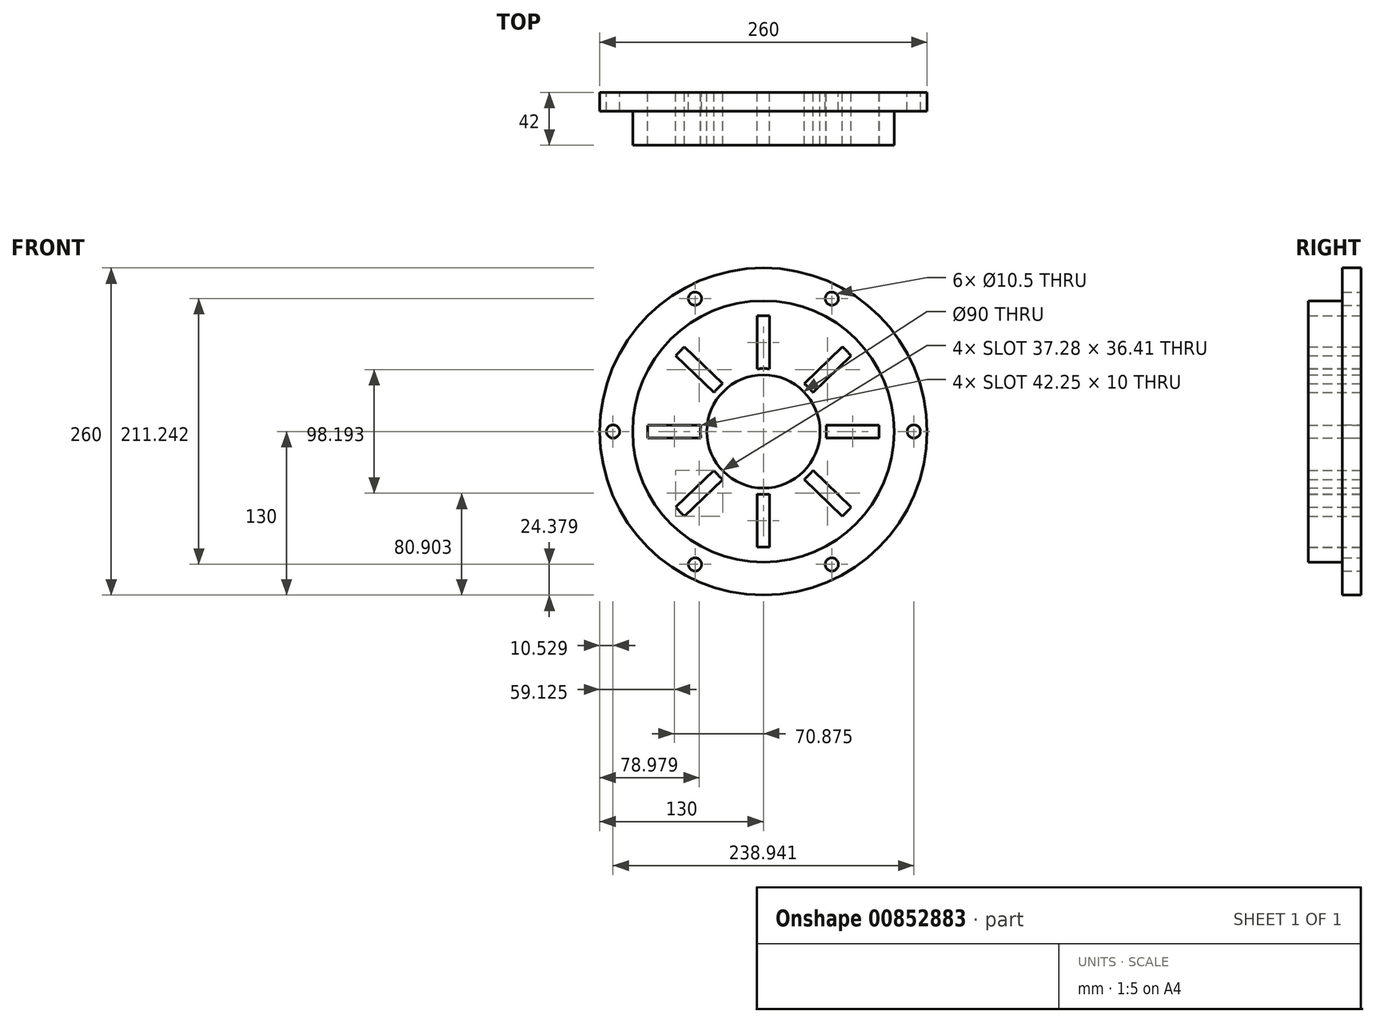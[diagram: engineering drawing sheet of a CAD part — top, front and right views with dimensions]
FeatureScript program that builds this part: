
annotation { "Feature Type Name" : "Feature", "Feature Type Description" : "" }
export const myFeature = defineFeature(function(context is Context, id is Id, definition is map)
    precondition{}
    {
        {
            var Q0;
            Q0=qCreatedBy(makeId("Front.planeOp"),FACE);
            var sketch = newSketch(context, id + "F0", { "sketchPlane" : qUnion([Q0])});
            skCircle(sketch, "E0", {"center": v(0, 0) * mm, "radius": 45 * mm});
            skCircle(sketch, "E1", {"center": v(0, 0) * mm, "radius": 50 * mm});
            skCircle(sketch, "E2", {"center": v(0, 0) * mm, "radius": 92 * mm});
            skCircle(sketch, "E3", {"center": v(0, 0) * mm, "radius": 95 * mm});
            skCircle(sketch, "E4", {"center": v(0, 0) * mm, "radius": 103.9 * mm});
            skCircle(sketch, "E5", {"center": v(0, 0) * mm, "radius": 130 * mm});
            skCircle(sketch, "E6", {"center": v(-54.3, 105.62) * mm, "radius": 5.25 * mm});
            skCircle(sketch, "E7.MirrorC", {"center": v(54.3, 105.62) * mm, "radius": 5.25 * mm});
            skCircle(sketch, "E8.MirrorC", {"center": v(-54.3, -105.62) * mm, "radius": 5.25 * mm});
            skCircle(sketch, "E9.MirrorC", {"center": v(54.3, -105.62) * mm, "radius": 5.25 * mm});
            skLineSegment(sketch, "E10", {"start": v(5, -49.75) * mm, "end": v(5, -91.86) * mm});
            skLineSegment(sketch, "E11.MirrorCS", {"start": v(5, 49.75) * mm, "end": v(5, 91.86) * mm});
            skLineSegment(sketch, "E12.MirrorCS", {"start": v(-5, -49.75) * mm, "end": v(-5, -91.86) * mm});
            skLineSegment(sketch, "E13.MirrorCS", {"start": v(-5, 49.75) * mm, "end": v(-5, 91.86) * mm});
            skLineSegment(sketch, "E14", {"start": v(-49.75, 5) * mm, "end": v(-91.86, 5) * mm});
            skLineSegment(sketch, "E15.MirrorCS", {"start": v(-49.75, -5) * mm, "end": v(-91.86, -5) * mm});
            skLineSegment(sketch, "E16.MirrorCS", {"start": v(49.75, 5) * mm, "end": v(91.86, 5) * mm});
            skLineSegment(sketch, "E17.MirrorCS", {"start": v(49.75, -5) * mm, "end": v(91.86, -5) * mm});
            skLineSegment(sketch, "E18", {"start": v(-32.38, 38.1) * mm, "end": v(-62.73, 67.3) * mm});
            skLineSegment(sketch, "E19", {"start": v(-39.31, 30.9) * mm, "end": v(-69.66, 60.1) * mm});
            skLineSegment(sketch, "E20.MirrorCS", {"start": v(-39.31, -30.9) * mm, "end": v(-69.66, -60.1) * mm});
            skLineSegment(sketch, "E21.MirrorCS", {"start": v(-32.38, -38.1) * mm, "end": v(-62.73, -67.3) * mm});
            skLineSegment(sketch, "E22.MirrorCS", {"start": v(32.38, 38.1) * mm, "end": v(62.73, 67.3) * mm});
            skLineSegment(sketch, "E23.MirrorCS", {"start": v(39.31, 30.9) * mm, "end": v(69.66, 60.1) * mm});
            skLineSegment(sketch, "E24.MirrorCS", {"start": v(39.31, -30.9) * mm, "end": v(69.66, -60.1) * mm});
            skLineSegment(sketch, "E25.MirrorCS", {"start": v(32.38, -38.1) * mm, "end": v(62.73, -67.3) * mm});
            skCircle(sketch, "E26", {"center": v(-119.47, 0) * mm, "radius": 5.25 * mm});
            skCircle(sketch, "E27.MirrorC", {"center": v(119.47, 0) * mm, "radius": 5.25 * mm});
            skSolve(sketch);
        }
        {
            var Q0;
            Q0=makeQuery(id+"F0.imprint","IMPRINT",FACE,{"disambiguationData":[TD([[makeQuery(id+"F0.imprint","IMPRINT",EDGE,{"derivedFrom":sQuery(id+"F0.wireOp",EDGE,"E4")}),-1.0]])]});
            extrude(context, id + "F1", {"entities" : qUnion([Q0]), "depth" : 15 * mm, "offsetDistance" : 25 * mm});
        }
        {
            var Q0;
            Q0=makeQuery(id+"F0.imprint","IMPRINT",FACE,{"disambiguationData":[TD([[makeQuery(id+"F0.imprint","IMPRINT",EDGE,{"derivedFrom":sQuery(id+"F0.wireOp",EDGE,"E3")}),-1.0]])]});
            var Q1;
            {var subQ0=sQuery(id+"F0.wireOp",EDGE,"E16.MirrorCS");Q1=makeQuery(id+"F0.imprint","IMPRINT",FACE,{"disambiguationData":[TD([[makeQuery(id+"F0.imprint","IMPRINT",EDGE,{"derivedFrom":subQ0}),1.0]])]});}
            var Q2;
            {var subQ0=sQuery(id+"F0.wireOp",EDGE,"E11.MirrorCS");Q2=makeQuery(id+"F0.imprint","IMPRINT",FACE,{"disambiguationData":[TD([[makeQuery(id+"F0.imprint","IMPRINT",EDGE,{"derivedFrom":subQ0}),-1.0]])]});}
            var Q3;
            {var subQ0=sQuery(id+"F0.wireOp",EDGE,"E13.MirrorCS");Q3=makeQuery(id+"F0.imprint","IMPRINT",FACE,{"disambiguationData":[TD([[makeQuery(id+"F0.imprint","IMPRINT",EDGE,{"derivedFrom":subQ0}),1.0]])]});}
            var Q4;
            {var subQ0=sQuery(id+"F0.wireOp",EDGE,"E14");Q4=makeQuery(id+"F0.imprint","IMPRINT",FACE,{"disambiguationData":[TD([[makeQuery(id+"F0.imprint","IMPRINT",EDGE,{"derivedFrom":subQ0}),-1.0]])]});}
            var Q5;
            {var subQ0=sQuery(id+"F0.wireOp",EDGE,"E15.MirrorCS");Q5=makeQuery(id+"F0.imprint","IMPRINT",FACE,{"disambiguationData":[TD([[makeQuery(id+"F0.imprint","IMPRINT",EDGE,{"derivedFrom":subQ0}),1.0]])]});}
            var Q6;
            {var subQ0=sQuery(id+"F0.wireOp",EDGE,"E12.MirrorCS");Q6=makeQuery(id+"F0.imprint","IMPRINT",FACE,{"disambiguationData":[TD([[makeQuery(id+"F0.imprint","IMPRINT",EDGE,{"derivedFrom":subQ0}),-1.0]])]});}
            var Q7;
            {var subQ0=sQuery(id+"F0.wireOp",EDGE,"E10");Q7=makeQuery(id+"F0.imprint","IMPRINT",FACE,{"disambiguationData":[TD([[makeQuery(id+"F0.imprint","IMPRINT",EDGE,{"derivedFrom":subQ0}),1.0]])]});}
            var Q8;
            {var subQ0=sQuery(id+"F0.wireOp",EDGE,"E17.MirrorCS");Q8=makeQuery(id+"F0.imprint","IMPRINT",FACE,{"disambiguationData":[TD([[makeQuery(id+"F0.imprint","IMPRINT",EDGE,{"derivedFrom":subQ0}),-1.0]])]});}
            var Q9;
            Q9=makeQuery(id+"F0.imprint","IMPRINT",FACE,{"disambiguationData":[TD([[makeQuery(id+"F0.imprint","IMPRINT",EDGE,{"derivedFrom":sQuery(id+"F0.wireOp",EDGE,"E0")}),-1.0]])]});
            var Q10;
            Q10=makeQuery(id+"F0.imprint","IMPRINT",FACE,{"disambiguationData":[TD([[makeQuery(id+"F0.imprint","IMPRINT",EDGE,{"derivedFrom":sQuery(id+"F0.wireOp",EDGE,"E3")}),1.0]])]});
            extrude(context, id + "F2", {"entities" : qUnion([Q0, Q1, Q2, Q3, Q4, Q5, Q6, Q7, Q8, Q9, Q10]), "operationType" : NewBodyOperationType.ADD, "depth" : 42 * mm, "offsetDistance" : 25 * mm});
        }
    });
